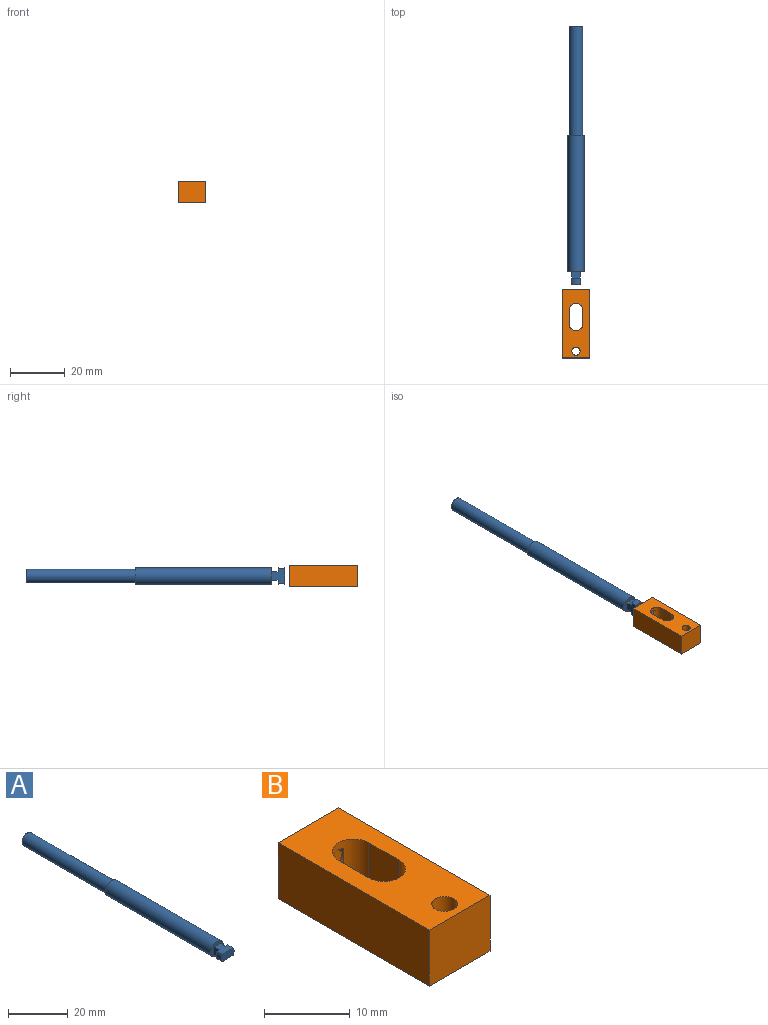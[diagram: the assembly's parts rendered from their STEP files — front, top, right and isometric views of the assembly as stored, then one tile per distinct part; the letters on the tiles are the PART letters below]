
ASSEMBLY  parts=2 mates=1
PART A: 14 faces, bbox 6x95x6 mm
  f0: plane 3x2.5mm, normal (-1,0,0), area 7.5mm2, adj f3,f5,f6,f11
  f1: plane 3x2.5mm, normal (1,0,0), area 7.5mm2, adj f3,f5,f6,f9
  f2: cylinder r=3mm len=50mm, axis (0,1,0), area 942.5mm2, adj f3,f4
  f3: plane 6x6mm, normal (0,-1,0), area 19.3mm2, adj f0,f1,f2,f5,f6
  f4: plane 6x6mm, normal (0,1,0), area 8.6mm2, adj f2,f12
  f5: plane 5.2x5mm, normal (0,0,1), area 20.5mm2, adj f0,f1,f3,f7,f8,f9,f10,f11
  f6: plane 5.2x5mm, normal (0,0,-1), area 20.5mm2, adj f0,f1,f3,f7,f8,f9,f10,f11
  f7: plane 6x3mm, normal (0,-1,0), area 17.2mm2, adj f5,f6,f8,f10
  f8: cylinder r=3mm len=3mm, axis (0,1,0), area 7.9mm2, adj f5,f6,f7,f9
  f9: plane 3x1.5mm, normal (0,1,0), area 4.1mm2, adj f1,f5,f6,f8
  f10: cylinder r=3mm len=3mm, axis (0,1,0), area 7.9mm2, adj f5,f6,f7,f11
  f11: plane 3x1.5mm, normal (0,1,0), area 4.1mm2, adj f0,f5,f6,f10
  f12: cylinder r=2.5mm len=40mm, axis (0,-1,0), area 628.3mm2, adj f4,f13
  f13: plane 5x5mm, normal (0,1,0), area 19.6mm2, adj f12
PART B: 21 faces, bbox 10x25x8 mm
  f0: plane 25x10mm, normal (0,0,1), area 198.3mm2, adj f7,f10,f12,f15,f16,f17,f18,f19
  f1: plane 25x10mm, normal (0,0,-1), area 198.3mm2, adj f7,f10,f12,f15,f16,f17,f18,f19
  f2: cylinder r=3mm len=5.1mm, axis (0,1,0), area 28.2mm2, adj f4,f5,f8,f9,f11,f12,f14,f19
  f3: cylinder r=3mm len=5.1mm, axis (0,1,0), area 28.2mm2, adj f4,f5,f6,f8,f9,f12,f13,f19
  f4: plane 5.83x2.3mm, normal (0,1,0), area 9.3mm2, adj f2,f3,f9,f14,f19
  f5: plane 5.83x2.3mm, normal (0,1,0), area 9.3mm2, adj f2,f3,f8,f13,f19
  f6: plane 4.1x1.5mm, normal (0,-1,0), area 4.8mm2, adj f3,f8,f13
  f7: plane 25x8mm, normal (-1,0,0), area 200mm2, adj f0,f1,f12,f15
  f8: plane 5.2x5.1mm, normal (1,0,0), area 15.8mm2, adj f2,f3,f5,f6,f12,f13
  f9: plane 5.2x5.1mm, normal (-1,0,0), area 15.8mm2, adj f2,f3,f4,f11,f12,f14
  f10: plane 25x8mm, normal (1,0,0), area 200mm2, adj f0,f1,f12,f15
  f11: plane 4.1x1.5mm, normal (0,-1,0), area 4.8mm2, adj f2,f9,f14
  f12: plane 10x8mm, normal (0,1,0), area 62.8mm2, adj f0,f1,f2,f3,f7,f8,f9,f10
  f13: plane 2.6x1.1mm, normal (0,0,1), area 2.9mm2, adj f3,f5,f6,f8
  f14: plane 2.6x1.1mm, normal (0,0,-1), area 2.9mm2, adj f2,f4,f9,f11
  f15: plane 10x8mm, normal (0,-1,0), area 80mm2, adj f0,f1,f7,f10
  f16: plane 8x5mm, normal (-1,0,0), area 40mm2, adj f0,f1,f18,f19
  f17: plane 8x5mm, normal (1,0,0), area 40mm2, adj f0,f1,f18,f19
  f18: cylinder r=2.5mm len=8mm, axis (0,0,1), area 62.8mm2, adj f0,f1,f16,f17
  f19: cylinder r=2.5mm len=8mm, axis (0,0,1), area 54.4mm2, adj f0,f1,f2,f3,f4,f5,f16,f17
  f20: cylinder r=1.5mm len=8mm, axis (0,0,1), area 75.4mm2, adj f0,f1
PLACE A rot(axis=(0,1,0),90deg) t=(0,56.8,13)mm
PLACE B at identity fixed
MATE cylindrical B.f2 <-> A.f2  axis (0,1,0) through (0,0,13)mm
